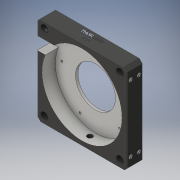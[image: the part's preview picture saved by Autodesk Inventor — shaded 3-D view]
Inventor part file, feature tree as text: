
AUTODESK INVENTOR PART (.ipt)
format: ipt  version: 2016 (Build 200138000, 138)  size: 1,051,136 bytes
history: native  units: in
note: dims shown in document units (in); Inventor stores cm internally (conversion verified against a paired STEP export)
features: other x9, sketch x5, extrude x4, projected_geometry x4, plane x1, hole x1, pattern_circular x1
ambient origin geometry x8: Origin, YZ Plane, XZ Plane, XY Plane, X Axis, Y Axis, Z Axis, Center Point
bodies: Solid1 (feature_tree), Solid2 (feature_tree), Solid3 (feature_tree), Solid4 (feature_tree), Solid5 (feature_tree), Solid6 (feature_tree), Solid7 (feature_tree), Solid8 (feature_tree), Solid9 (feature_tree)
feature tree (25):
  plane  "Work Plane1"
  extrude  "Extrusion2"  [1 undecoded]
  extrude  "Extrusion1"  Depth=1.0in TaperAngle=0.0deg
  extrude  "Extrusion5"  Depth=0.4in
  hole  "Hole1"  [1 undecoded]
  pattern_circular  "Circular Pattern1"  Count=5 Angle=360.0deg
  extrude  "Extrusion6"  Depth=0.25in
  sketch  "Sketch2"  dims[d1=2.5in d2=-0.0787in]
  projected_geometry  "Projected Loop2"
  sketch  "Sketch4"  dims[d3=1.0in d4=0.0in d5=1.0in d6=0.0in]
  sketch  "Sketch7"  dims[d17=0.475in d18=0.4in]
  projected_geometry  "Projected Loop8"
  sketch  "Sketch8"  dims[d19=1.25in d20=1.0in d21=0.0in]
  projected_geometry  "Projected Loop9"
  sketch  "Sketch9"  dims[d22=2.12in d23=0.067in d24=0.172in d25=0.375in d26=0.25in d27=0.5635in d28=0.261in d29=0.8108in d30=1.9685in d31=360.0deg d33=0.0618in d34=1.0in d35=0.0in]
  projected_geometry  "Projected Loop10"
  other  "13107-001-1-solid1"
  other  "SS4S019-1-1-solid1"
  other  "SS4S019-1-2-solid1"
  other  "SS4S019-1-3-solid1"
  other  "SS4S019-1-4-solid1"
  other  "SS4S019-1-5-solid1"
  other  "SS4S019-1-6-solid1"
  other  "SS4S019-1-7-solid1"
  other  "SS4S019-1-8-solid1"
note: 2 required parameter values undecoded (feature->parameter linkage not recoverable at this tier; creation-order binding heuristic only, values carry confidence <= 0.55)
